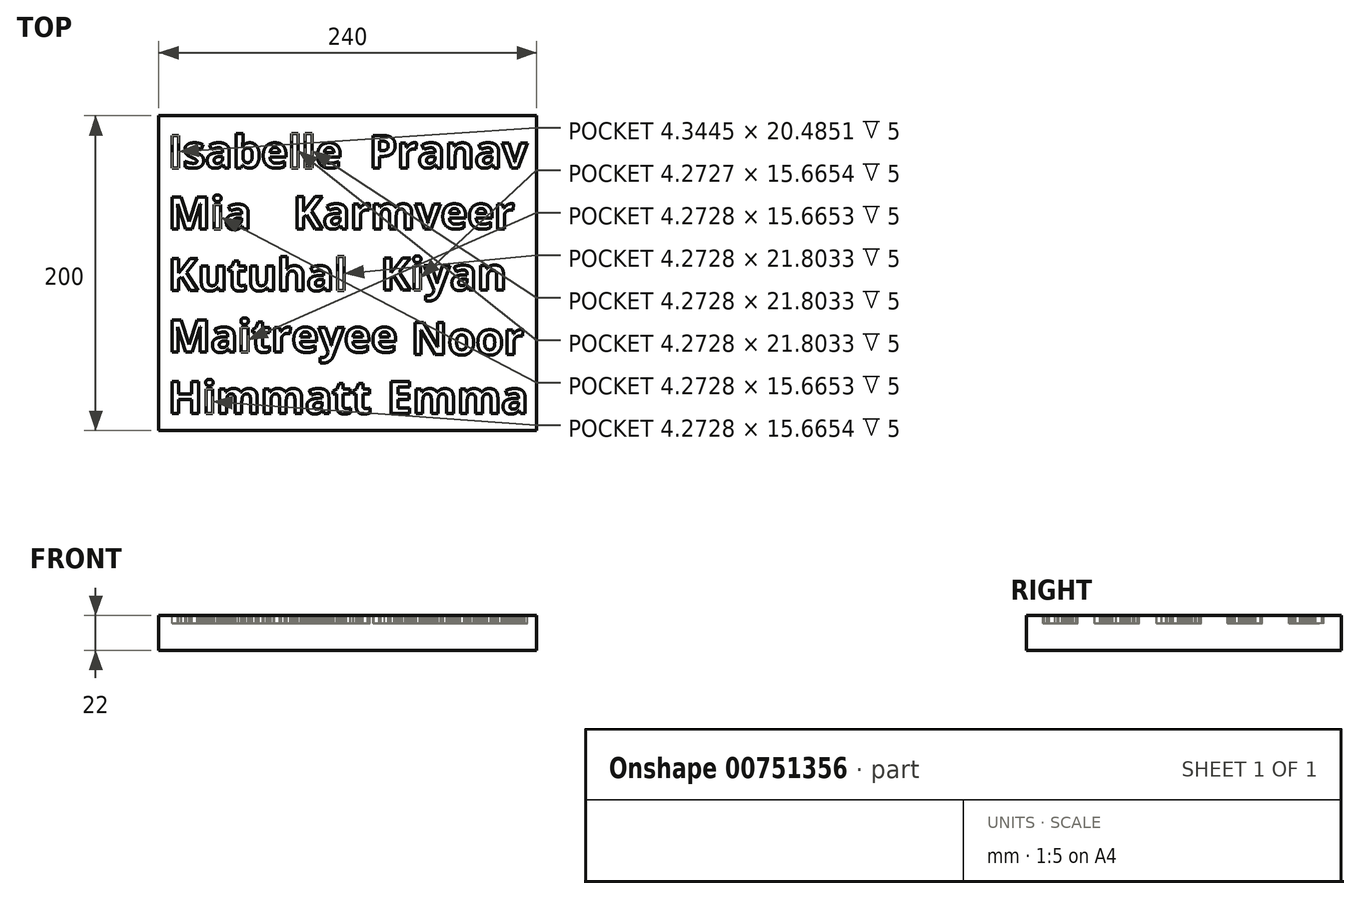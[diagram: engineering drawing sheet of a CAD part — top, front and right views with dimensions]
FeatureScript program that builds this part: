
annotation { "Feature Type Name" : "Feature", "Feature Type Description" : "" }
export const myFeature = defineFeature(function(context is Context, id is Id, definition is map)
    precondition{}
    {
        {
            var Q0;
            Q0=qCreatedBy(makeId("Top.planeOp"),FACE);
            var sketch = newSketch(context, id + "F0", { "sketchPlane" : qUnion([Q0])});
            skLineSegment(sketch, "E0.bottom", {"start": v(-118.17, 158.27) * mm, "end": v(121.83, 158.27) * mm});
            skLineSegment(sketch, "E0.top", {"start": v(-118.17, -41.73) * mm, "end": v(121.83, -41.73) * mm});
            skLineSegment(sketch, "E0.left", {"start": v(-118.17, 158.27) * mm, "end": v(-118.17, -41.73) * mm});
            skLineSegment(sketch, "E0.right", {"start": v(121.83, 158.27) * mm, "end": v(121.83, -41.73) * mm});
            skSolve(sketch);
        }
        {
            var Q0;
            Q0=makeQuery(id+"F0.imprint","IMPRINT",FACE,{"disambiguationData":[TD([[makeQuery(id+"F0.imprint","IMPRINT",EDGE,{"derivedFrom":sQuery(id+"F0.wireOp",EDGE,"E0.bottom")}),-1.0]])]});
            extrude(context, id + "F1", {"entities" : qUnion([Q0]), "depth" : 22 * mm, "offsetDistance" : 25 * mm});
        }
        {
            var Q0;
            Q0=makeQuery(id+"F1.opExtrude","CAP_FACE",FACE,{"disambiguationData":[OSD([sQuery(id+"F0.wireOp",EDGE,"E0.bottom"),sQuery(id+"F0.wireOp",EDGE,"E0.top"),sQuery(id+"F0.wireOp",EDGE,"E0.left"),sQuery(id+"F0.wireOp",EDGE,"E0.right")])],"isStart":false});
            var sketch = newSketch(context, id + "F2", { "sketchPlane" : qUnion([Q0])});
            skText(sketch, "E1", { "text": "Isabelle\nMia\nKutuhal\nMaitreyee\nHimmatt", "fontName": "OpenSans-Bold.ttf"});
            skText(sketch, "E2", { "text": "Noor", "fontName": "OpenSans-Bold.ttf"});
            skText(sketch, "E3", { "text": "Pranav", "fontName": "OpenSans-Bold.ttf"});
            skText(sketch, "E4", { "text": "Karmveer", "fontName": "OpenSans-Bold.ttf"});
            skText(sketch, "E5", { "text": "Kiyan", "fontName": "OpenSans-Bold.ttf"});
            skText(sketch, "E6", { "text": "Emma", "fontName": "OpenSans-Bold.ttf"});
            const initialGuessF2  = {"E1": [-0.1124, 0.12516, 1, 0, 0.02066], "E2": [0.04202, 0.00644, 1, 0, 0.02066], "E3": [0.0152, 0.12516, 1, 0, 0.02066], "E4": [-0.03306, 0.08644, 1, 0, 0.02066], "E5": [0.02256, 0.04744, 1, 0, 0.02066], "E6": [0.02685, -0.031, 1, 0, 0.02066]};
            skSetInitialGuess(sketch, initialGuessF2);
            skSolve(sketch);
        }
        {
            var Q0;
            Q0 = qSketchRegion(id + "F2", true);
            extrude(context, id + "F3", {"entities" : qUnion([Q0]), "operationType" : NewBodyOperationType.REMOVE, "oppositeDirection" : true, "depth" : 5 * mm, "offsetDistance" : 25 * mm});
        }
    });
